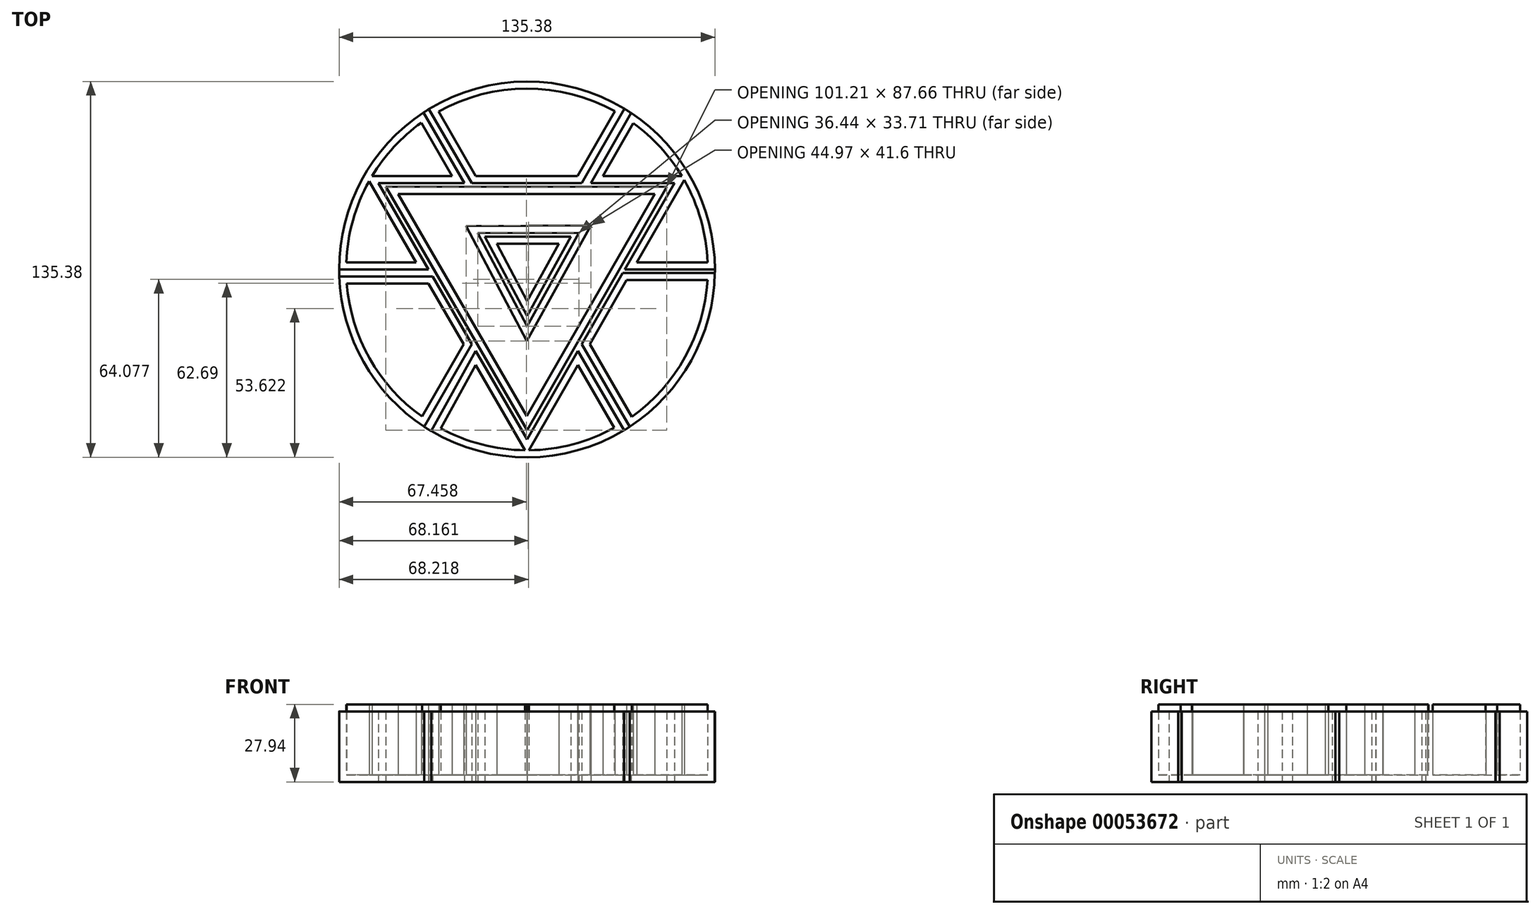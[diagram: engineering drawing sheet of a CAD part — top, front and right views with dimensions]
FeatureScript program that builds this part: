
annotation { "Feature Type Name" : "Feature", "Feature Type Description" : "" }
export const myFeature = defineFeature(function(context is Context, id is Id, definition is map)
    precondition{}
    {
        {
            var Q0;
            Q0=qCreatedBy(makeId("Top.planeOp"),FACE);
            var sketch = newSketch(context, id + "F0", { "sketchPlane" : qUnion([Q0])});
            skCircle(sketch, "E0", {"center": v(0, 0) * mm, "radius": 67.7 * mm});
            skLineSegment(sketch, "E1", {"start": v(-53.57, 31.14) * mm, "end": v(0, -61.24) * mm});
            skLineSegment(sketch, "E2", {"start": v(0, -61.24) * mm, "end": v(53.1, 31.14) * mm});
            skLineSegment(sketch, "E3", {"start": v(53.1, 31.14) * mm, "end": v(-53.57, 31.14) * mm});
            skLineSegment(sketch, "E4", {"start": v(-15.13, 11.77) * mm, "end": v(0, -16.84) * mm});
            skLineSegment(sketch, "E5", {"start": v(0, -16.84) * mm, "end": v(15.86, 11.77) * mm});
            skLineSegment(sketch, "E6", {"start": v(15.86, 11.77) * mm, "end": v(-15.13, 11.77) * mm});
            skLineSegment(sketch, "E7", {"start": v(-15.13, 11.77) * mm, "end": v(-53.57, 31.14) * mm});
            skLineSegment(sketch, "E8", {"start": v(15.86, 11.77) * mm, "end": v(53.1, 31.14) * mm});
            skLineSegment(sketch, "E9", {"start": v(0, -16.84) * mm, "end": v(0, -61.24) * mm});
            skLineSegment(sketch, "E10", {"start": v(-35.51, 0) * mm, "end": v(-67.7, 0) * mm});
            skLineSegment(sketch, "E11", {"start": v(35.2, 0) * mm, "end": v(67.7, 0) * mm});
            skLineSegment(sketch, "E12", {"start": v(-19.9, -26.92) * mm, "end": v(-37, -56.68) * mm});
            skLineSegment(sketch, "E13", {"start": v(19.73, -26.92) * mm, "end": v(37, -56.68) * mm});
            skLineSegment(sketch, "E14", {"start": v(-19.9, 31.14) * mm, "end": v(-35.33, 57.74) * mm});
            skLineSegment(sketch, "E15", {"start": v(19.73, 31.14) * mm, "end": v(35.1, 57.88) * mm});
            skLineSegment(sketch, "E16", {"start": v(-17.75, 13.09) * mm, "end": v(0, -20.47) * mm});
            skLineSegment(sketch, "E17", {"start": v(0, -20.47) * mm, "end": v(18.69, 13.24) * mm});
            skLineSegment(sketch, "E18", {"start": v(18.69, 13.24) * mm, "end": v(-17.75, 13.09) * mm});
            skLineSegment(sketch, "E19", {"start": v(-50.83, 29.76) * mm, "end": v(0, -57.9) * mm});
            skLineSegment(sketch, "E20", {"start": v(0, -57.9) * mm, "end": v(50.37, 29.72) * mm});
            skLineSegment(sketch, "E21", {"start": v(50.37, 29.72) * mm, "end": v(-50.83, 29.76) * mm});
            skLineSegment(sketch, "E22", {"start": v(-18.5, -29.35) * mm, "end": v(-34.5, -58.24) * mm});
            skLineSegment(sketch, "E23", {"start": v(34.43, -1.34) * mm, "end": v(67.68, -1.34) * mm});
            skLineSegment(sketch, "E24", {"start": v(-35.51, -2.53) * mm, "end": v(-67.7, -2.53) * mm});
            skPoint(sketch, "E24.startSnap0", {"position": v(-7.56, -2.53) * mm});
            skLineSegment(sketch, "E25", {"start": v(-67.7, -2.53) * mm, "end": v(-34.04, -2.53) * mm});
            skLineSegment(sketch, "E26", {"start": v(-22.58, 31.14) * mm, "end": v(-37.29, 56.5) * mm});
            skLineSegment(sketch, "E27", {"start": v(23.01, 31.14) * mm, "end": v(37.5, 56.35) * mm});
            skLineSegment(sketch, "E28", {"start": v(18.33, -29.35) * mm, "end": v(34.95, -57.97) * mm});
            skSolve(sketch);
        }
        {
            var Q0;
            {var subQ0=sQuery(id+"F0.wireOp",EDGE,"E22");Q0=makeQuery(id+"F0.imprint","IMPRINT",FACE,{"disambiguationData":[TD([[makeQuery(id+"F0.imprint","IMPRINT",EDGE,{"derivedFrom":subQ0}),1.0]])]});}
            var Q1;
            {var subQ0=sQuery(id+"F0.wireOp",EDGE,"E13");Q1=makeQuery(id+"F0.imprint","IMPRINT",FACE,{"disambiguationData":[TD([[makeQuery(id+"F0.imprint","IMPRINT",EDGE,{"derivedFrom":subQ0}),1.0]])]});}
            var Q2;
            {var subQ0=sQuery(id+"F0.wireOp",EDGE,"E11");Q2=makeQuery(id+"F0.imprint","IMPRINT",FACE,{"disambiguationData":[TD([[makeQuery(id+"F0.imprint","IMPRINT",EDGE,{"derivedFrom":subQ0}),1.0]])]});}
            var Q3;
            {var subQ0=sQuery(id+"F0.wireOp",EDGE,"E14");Q3=makeQuery(id+"F0.imprint","IMPRINT",FACE,{"disambiguationData":[TD([[makeQuery(id+"F0.imprint","IMPRINT",EDGE,{"derivedFrom":subQ0}),-1.0]])]});}
            var Q4;
            {var subQ0=sQuery(id+"F0.wireOp",EDGE,"E10");Q4=makeQuery(id+"F0.imprint","IMPRINT",FACE,{"disambiguationData":[TD([[makeQuery(id+"F0.imprint","IMPRINT",EDGE,{"derivedFrom":subQ0}),-1.0]])]});}
            var Q5;
            {var subQ4=sQuery(id+"F0.wireOp",EDGE,"E12");Q5=makeQuery(id+"F0.imprint","IMPRINT",FACE,{"disambiguationData":[TD([[makeQuery(id+"F0.imprint","IMPRINT",EDGE,{"derivedFrom":subQ4}),-1.0]])]});}
            var Q6;
            {var subQ0=sQuery(id+"F0.wireOp",EDGE,"E16");Q6=makeQuery(id+"F0.imprint","IMPRINT",FACE,{"disambiguationData":[TD([[makeQuery(id+"F0.imprint","IMPRINT",EDGE,{"derivedFrom":subQ0}),-1.0]])]});}
            var Q7;
            {var subQ0=sQuery(id+"F0.wireOp",EDGE,"E17");Q7=makeQuery(id+"F0.imprint","IMPRINT",FACE,{"disambiguationData":[TD([[makeQuery(id+"F0.imprint","IMPRINT",EDGE,{"derivedFrom":subQ0}),-1.0]])]});}
            var Q8;
            {var subQ0=sQuery(id+"F0.wireOp",EDGE,"E18");Q8=makeQuery(id+"F0.imprint","IMPRINT",FACE,{"disambiguationData":[TD([[makeQuery(id+"F0.imprint","IMPRINT",EDGE,{"derivedFrom":subQ0}),-1.0]])]});}
            var Q9;
            Q9=makeQuery(id+"F0.imprint","IMPRINT",FACE,{"disambiguationData":[TD([[makeQuery(id+"F0.imprint","IMPRINT",EDGE,{"derivedFrom":sQuery(id+"F0.wireOp",EDGE,"E4")}),1.0]])]});
            extrude(context, id + "F1", {"entities" : qUnion([Q0, Q1, Q2, Q3, Q4, Q5, Q6, Q7, Q8, Q9]), "depth" : 25.4 * mm});
        }
        {
            var Q0;
            Q0=makeQuery(id+"F1.opExtrude","CAP_FACE",FACE,{"disambiguationData":[OSD([sQuery(id+"F0.wireOp",EDGE,"E0"),sQuery(id+"F0.wireOp",EDGE,"E1"),sQuery(id+"F0.wireOp",EDGE,"E2"),sQuery(id+"F0.wireOp",EDGE,"E22"),sQuery(id+"F0.wireOp",EDGE,"E28")])],"isStart":false});
            var Q1;
            Q1=makeQuery(id+"F1.opExtrude","CAP_FACE",FACE,{"disambiguationData":[OSD([sQuery(id+"F0.wireOp",EDGE,"E0"),sQuery(id+"F0.wireOp",EDGE,"E1"),sQuery(id+"F0.wireOp",EDGE,"E12"),sQuery(id+"F0.wireOp",EDGE,"E25")])],"isStart":false});
            var Q2;
            Q2=makeQuery(id+"F1.opExtrude","CAP_FACE",FACE,{"disambiguationData":[OSD([sQuery(id+"F0.wireOp",EDGE,"E0"),sQuery(id+"F0.wireOp",EDGE,"E1"),sQuery(id+"F0.wireOp",EDGE,"E3"),sQuery(id+"F0.wireOp",EDGE,"E10"),sQuery(id+"F0.wireOp",EDGE,"E26")])],"isStart":false});
            var Q3;
            Q3=makeQuery(id+"F1.opExtrude","CAP_FACE",FACE,{"disambiguationData":[OSD([sQuery(id+"F0.wireOp",EDGE,"E0"),sQuery(id+"F0.wireOp",EDGE,"E3"),sQuery(id+"F0.wireOp",EDGE,"E14"),sQuery(id+"F0.wireOp",EDGE,"E15")])],"isStart":false});
            var Q4;
            Q4=makeQuery(id+"F1.opExtrude","CAP_FACE",FACE,{"disambiguationData":[OSD([sQuery(id+"F0.wireOp",EDGE,"E0"),sQuery(id+"F0.wireOp",EDGE,"E2"),sQuery(id+"F0.wireOp",EDGE,"E3"),sQuery(id+"F0.wireOp",EDGE,"E11"),sQuery(id+"F0.wireOp",EDGE,"E27")])],"isStart":false});
            var Q5;
            Q5=makeQuery(id+"F1.opExtrude","CAP_FACE",FACE,{"disambiguationData":[OSD([sQuery(id+"F0.wireOp",EDGE,"E0"),sQuery(id+"F0.wireOp",EDGE,"E2"),sQuery(id+"F0.wireOp",EDGE,"E13"),sQuery(id+"F0.wireOp",EDGE,"E23")])],"isStart":false});
            var Q6;
            Q6=makeQuery(id+"F1.opExtrude","CAP_FACE",FACE,{"disambiguationData":[OSD([sQuery(id+"F0.wireOp",EDGE,"E16"),sQuery(id+"F0.wireOp",EDGE,"E17"),sQuery(id+"F0.wireOp",EDGE,"E18"),sQuery(id+"F0.wireOp",EDGE,"E19"),sQuery(id+"F0.wireOp",EDGE,"E20"),sQuery(id+"F0.wireOp",EDGE,"E21")])],"isStart":false});
            var Q7;
            Q7=makeQuery(id+"F1.opExtrude","CAP_FACE",FACE,{"disambiguationData":[OSD([sQuery(id+"F0.wireOp",EDGE,"E4"),sQuery(id+"F0.wireOp",EDGE,"E5"),sQuery(id+"F0.wireOp",EDGE,"E6")])],"isStart":false});
            shell(context, id + "F2", {"entities" : qUnion([Q0, Q1, Q2, Q3, Q4, Q5, Q6, Q7]), "thickness" : 2.54 * mm});
        }
        {
            var Q0;
            Q0=makeQuery(id+"F2.opShell","OFFSET_FACE",FACE,{"disambiguationData":[OSD([sQuery(id+"F0.wireOp",EDGE,"E0"),sQuery(id+"F0.wireOp",EDGE,"E1"),sQuery(id+"F0.wireOp",EDGE,"E12"),sQuery(id+"F0.wireOp",EDGE,"E25")])]});
            var Q1;
            Q1=makeQuery(id+"F2.opShell","OFFSET_FACE",FACE,{"disambiguationData":[OSD([sQuery(id+"F0.wireOp",EDGE,"E0"),sQuery(id+"F0.wireOp",EDGE,"E1"),sQuery(id+"F0.wireOp",EDGE,"E2"),sQuery(id+"F0.wireOp",EDGE,"E22"),sQuery(id+"F0.wireOp",EDGE,"E28")]),OD(0.0)]});
            var Q2;
            Q2=makeQuery(id+"F2.opShell","OFFSET_FACE",FACE,{"disambiguationData":[OSD([sQuery(id+"F0.wireOp",EDGE,"E0"),sQuery(id+"F0.wireOp",EDGE,"E1"),sQuery(id+"F0.wireOp",EDGE,"E2"),sQuery(id+"F0.wireOp",EDGE,"E22"),sQuery(id+"F0.wireOp",EDGE,"E28")]),OD(1.0)]});
            var Q3;
            Q3=makeQuery(id+"F2.opShell","OFFSET_FACE",FACE,{"disambiguationData":[OSD([sQuery(id+"F0.wireOp",EDGE,"E0"),sQuery(id+"F0.wireOp",EDGE,"E2"),sQuery(id+"F0.wireOp",EDGE,"E13"),sQuery(id+"F0.wireOp",EDGE,"E23")])]});
            var Q4;
            {var subQ0=sQuery(id+"F0.wireOp",EDGE,"E21");var subQ1=sQuery(id+"F0.wireOp",EDGE,"E20");var subQ2=sQuery(id+"F0.wireOp",EDGE,"E19");var subQ3=sQuery(id+"F0.wireOp",EDGE,"E18");var subQ4=sQuery(id+"F0.wireOp",EDGE,"E17");var subQ5=sQuery(id+"F0.wireOp",EDGE,"E16");Q4=makeQuery(id+"F2.opShell","OFFSET_FACE",FACE,{"disambiguationData":[OSD([subQ5,subQ4,subQ3,subQ2,subQ1,subQ0]),TDD([makeQuery(id+"F1.opExtrude","CAP_FACE",FACE,{"disambiguationData":[OSD([subQ5,subQ4,subQ3,subQ2,subQ1,subQ0])],"isStart":true})])]});}
            var Q5;
            Q5=makeQuery(id+"F2.opShell","OFFSET_FACE",FACE,{"disambiguationData":[OSD([sQuery(id+"F0.wireOp",EDGE,"E4"),sQuery(id+"F0.wireOp",EDGE,"E5"),sQuery(id+"F0.wireOp",EDGE,"E6")])]});
            var Q6;
            Q6=makeQuery(id+"F2.opShell","OFFSET_FACE",FACE,{"disambiguationData":[OSD([sQuery(id+"F0.wireOp",EDGE,"E0"),sQuery(id+"F0.wireOp",EDGE,"E2"),sQuery(id+"F0.wireOp",EDGE,"E3"),sQuery(id+"F0.wireOp",EDGE,"E11"),sQuery(id+"F0.wireOp",EDGE,"E27")]),OD(0.0)]});
            var Q7;
            Q7=makeQuery(id+"F2.opShell","OFFSET_FACE",FACE,{"disambiguationData":[OSD([sQuery(id+"F0.wireOp",EDGE,"E0"),sQuery(id+"F0.wireOp",EDGE,"E2"),sQuery(id+"F0.wireOp",EDGE,"E3"),sQuery(id+"F0.wireOp",EDGE,"E11"),sQuery(id+"F0.wireOp",EDGE,"E27")]),OD(1.0)]});
            var Q8;
            Q8=makeQuery(id+"F2.opShell","OFFSET_FACE",FACE,{"disambiguationData":[OSD([sQuery(id+"F0.wireOp",EDGE,"E0"),sQuery(id+"F0.wireOp",EDGE,"E3"),sQuery(id+"F0.wireOp",EDGE,"E14"),sQuery(id+"F0.wireOp",EDGE,"E15")])]});
            var Q9;
            Q9=makeQuery(id+"F2.opShell","OFFSET_FACE",FACE,{"disambiguationData":[OSD([sQuery(id+"F0.wireOp",EDGE,"E0"),sQuery(id+"F0.wireOp",EDGE,"E1"),sQuery(id+"F0.wireOp",EDGE,"E3"),sQuery(id+"F0.wireOp",EDGE,"E10"),sQuery(id+"F0.wireOp",EDGE,"E26")]),OD(1.0)]});
            var Q10;
            Q10=makeQuery(id+"F2.opShell","OFFSET_FACE",FACE,{"disambiguationData":[OSD([sQuery(id+"F0.wireOp",EDGE,"E0"),sQuery(id+"F0.wireOp",EDGE,"E1"),sQuery(id+"F0.wireOp",EDGE,"E3"),sQuery(id+"F0.wireOp",EDGE,"E10"),sQuery(id+"F0.wireOp",EDGE,"E26")]),OD(0.0)]});
            extrude(context, id + "F3", {"entities" : qUnion([Q0, Q1, Q2, Q3, Q4, Q5, Q6, Q7, Q8, Q9, Q10]), "depth" : 25.4 * mm});
        }
        {
            var Q0;
            {var subQ4=sQuery(id+"F0.wireOp",EDGE,"E10");Q0=makeQuery(id+"F0.imprint","IMPRINT",FACE,{"disambiguationData":[TD([[makeQuery(id+"F0.imprint","IMPRINT",EDGE,{"derivedFrom":subQ4}),1.0]])]});}
            var Q1;
            {var subQ0=sQuery(id+"F0.wireOp",EDGE,"E12");Q1=makeQuery(id+"F0.imprint","IMPRINT",FACE,{"disambiguationData":[TD([[makeQuery(id+"F0.imprint","IMPRINT",EDGE,{"derivedFrom":subQ0}),1.0]])]});}
            var Q2;
            {var subQ0=sQuery(id+"F0.wireOp",EDGE,"E13");Q2=makeQuery(id+"F0.imprint","IMPRINT",FACE,{"disambiguationData":[TD([[makeQuery(id+"F0.imprint","IMPRINT",EDGE,{"derivedFrom":subQ0}),-1.0]])]});}
            var Q3;
            {var subQ0=sQuery(id+"F0.wireOp",EDGE,"E11");Q3=makeQuery(id+"F0.imprint","IMPRINT",FACE,{"disambiguationData":[TD([[makeQuery(id+"F0.imprint","IMPRINT",EDGE,{"derivedFrom":subQ0}),-1.0]])]});}
            var Q4;
            {var subQ7=sQuery(id+"F0.wireOp",EDGE,"E20");Q4=makeQuery(id+"F0.imprint","IMPRINT",FACE,{"disambiguationData":[TD([[makeQuery(id+"F0.imprint","IMPRINT",EDGE,{"derivedFrom":subQ7}),-1.0]])]});}
            var Q5;
            {var subQ0=sQuery(id+"F0.wireOp",EDGE,"E15");Q5=makeQuery(id+"F0.imprint","IMPRINT",FACE,{"disambiguationData":[TD([[makeQuery(id+"F0.imprint","IMPRINT",EDGE,{"derivedFrom":subQ0}),-1.0]])]});}
            var Q6;
            {var subQ0=sQuery(id+"F0.wireOp",EDGE,"E14");Q6=makeQuery(id+"F0.imprint","IMPRINT",FACE,{"disambiguationData":[TD([[makeQuery(id+"F0.imprint","IMPRINT",EDGE,{"derivedFrom":subQ0}),1.0]])]});}
            var Q7;
            {var subQ7=sQuery(id+"F0.wireOp",EDGE,"E19");Q7=makeQuery(id+"F0.imprint","IMPRINT",FACE,{"disambiguationData":[TD([[makeQuery(id+"F0.imprint","IMPRINT",EDGE,{"derivedFrom":subQ7}),-1.0]])]});}
            var Q8;
            {var subQ9=sQuery(id+"F0.wireOp",EDGE,"E21");Q8=makeQuery(id+"F0.imprint","IMPRINT",FACE,{"disambiguationData":[TD([[makeQuery(id+"F0.imprint","IMPRINT",EDGE,{"derivedFrom":subQ9}),-1.0]])]});}
            var Q9;
            {var subQ0=sQuery(id+"F0.wireOp",EDGE,"E4");Q9=makeQuery(id+"F0.imprint","IMPRINT",FACE,{"disambiguationData":[TD([[makeQuery(id+"F0.imprint","IMPRINT",EDGE,{"derivedFrom":subQ0}),-1.0]])]});}
            var Q10;
            {var subQ0=sQuery(id+"F0.wireOp",EDGE,"E5");Q10=makeQuery(id+"F0.imprint","IMPRINT",FACE,{"disambiguationData":[TD([[makeQuery(id+"F0.imprint","IMPRINT",EDGE,{"derivedFrom":subQ0}),-1.0]])]});}
            var Q11;
            {var subQ0=sQuery(id+"F0.wireOp",EDGE,"E6");Q11=makeQuery(id+"F0.imprint","IMPRINT",FACE,{"disambiguationData":[TD([[makeQuery(id+"F0.imprint","IMPRINT",EDGE,{"derivedFrom":subQ0}),-1.0]])]});}
            extrude(context, id + "F4", {"entities" : qUnion([Q0, Q1, Q2, Q3, Q4, Q5, Q6, Q7, Q8, Q9, Q10, Q11]), "depth" : 25.4 * mm});
        }
    });
